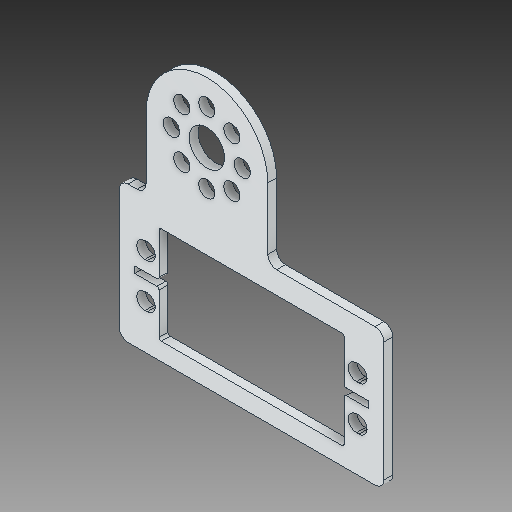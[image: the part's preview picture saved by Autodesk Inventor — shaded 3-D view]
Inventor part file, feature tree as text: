
AUTODESK INVENTOR PART (.ipt)
format: ipt  version: 2018 (Build 220112000, 112)  size: 180,224 bytes
history: native  units: in
note: dims shown in document units (in); Inventor stores cm internally (conversion verified against a paired STEP export)
features: fillet x1
ambient origin geometry x8: Origin, YZ Plane, XZ Plane, XY Plane, X Axis, Y Axis, Z Axis, Center Point
bodies: Solid1 (feature_tree)
feature tree (1):
  fillet  "Fillet2"  [1 undecoded]
note: 1 required parameter value undecoded (feature->parameter linkage not recoverable at this tier; creation-order binding heuristic only, values carry confidence <= 0.55)
